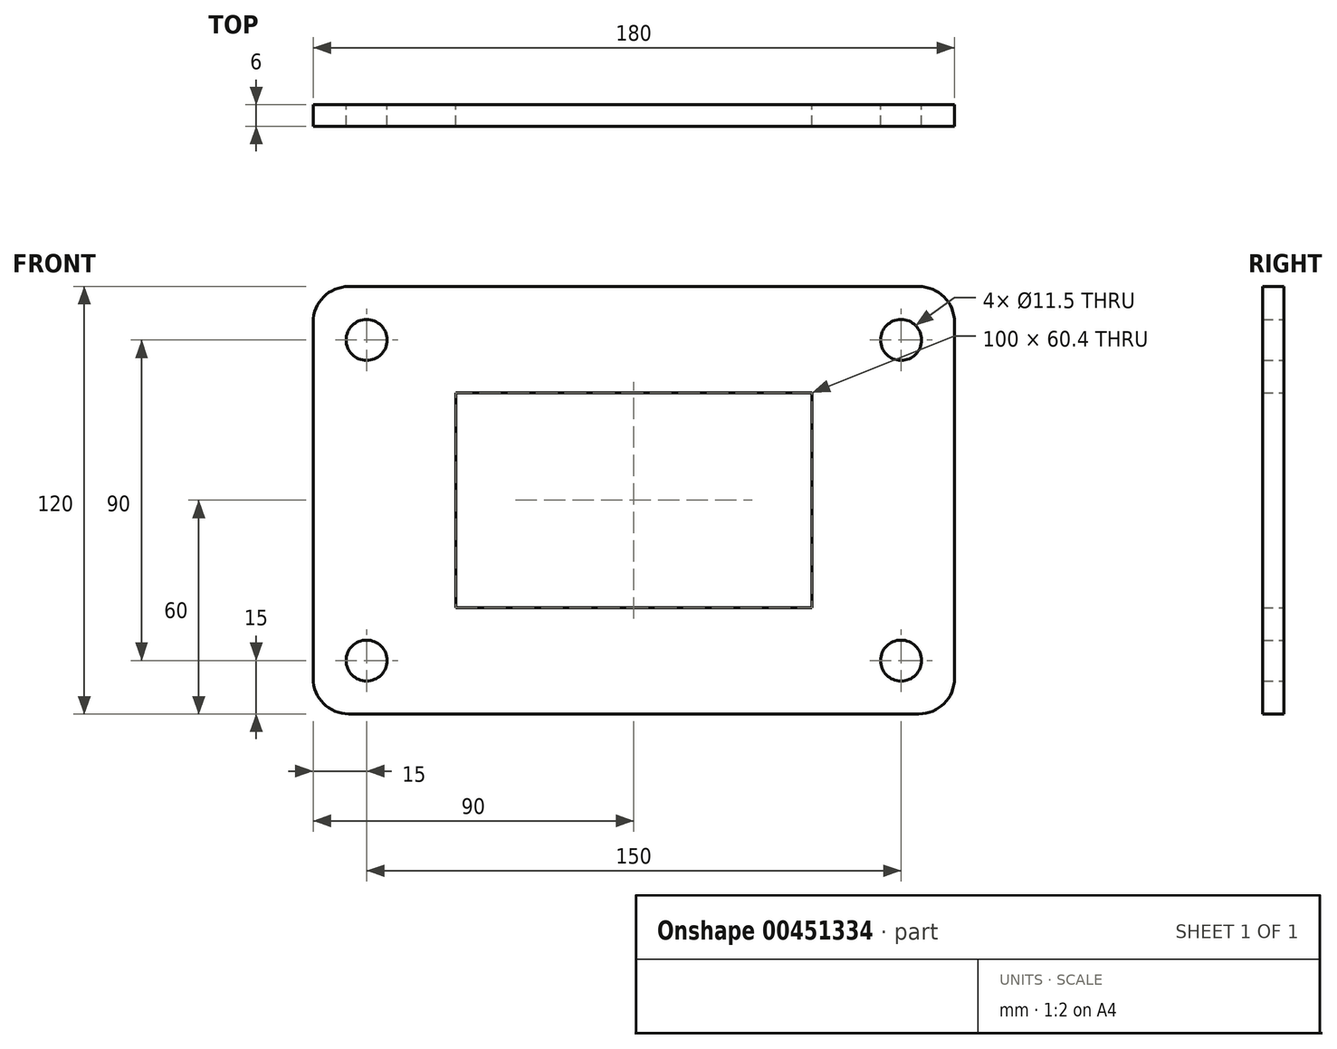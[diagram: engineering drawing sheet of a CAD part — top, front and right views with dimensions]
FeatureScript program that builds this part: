
annotation { "Feature Type Name" : "Feature", "Feature Type Description" : "" }
export const myFeature = defineFeature(function(context is Context, id is Id, definition is map)
    precondition{}
    {
        {
            var Q0;
            Q0=qCreatedBy(makeId("Front.planeOp"),FACE);
            var sketch = newSketch(context, id + "F0", { "sketchPlane" : qUnion([Q0])});
            skLineSegment(sketch, "E0.bottom", {"start": v(90, 60) * mm, "end": v(-90, 60) * mm});
            skLineSegment(sketch, "E0.top", {"start": v(90, -60) * mm, "end": v(-90, -60) * mm});
            skLineSegment(sketch, "E0.left", {"start": v(90, 60) * mm, "end": v(90, -60) * mm});
            skLineSegment(sketch, "E0.right", {"start": v(-90, 60) * mm, "end": v(-90, -60) * mm});
            skPoint(sketch, "E0.middle", {"position": v(0, 0) * mm});
            skLineSegment(sketch, "E1.bottom", {"start": v(50, 30.2) * mm, "end": v(-50, 30.2) * mm});
            skLineSegment(sketch, "E1.top", {"start": v(50, -30.2) * mm, "end": v(-50, -30.2) * mm});
            skLineSegment(sketch, "E1.left", {"start": v(50, 30.2) * mm, "end": v(50, -30.2) * mm});
            skLineSegment(sketch, "E1.right", {"start": v(-50, 30.2) * mm, "end": v(-50, -30.2) * mm});
            skCircle(sketch, "E2", {"center": v(-75, 45) * mm, "radius": 5.75 * mm});
            skCircle(sketch, "E3", {"center": v(-75, -45) * mm, "radius": 5.75 * mm});
            skCircle(sketch, "E4.MirrorC", {"center": v(75, -45) * mm, "radius": 5.75 * mm});
            skCircle(sketch, "E5.MirrorC", {"center": v(75, 45) * mm, "radius": 5.75 * mm});
            skSolve(sketch);
        }
        {
            var Q0;
            Q0=makeQuery(id+"F0.imprint","IMPRINT",FACE,{"disambiguationData":[TD([[makeQuery(id+"F0.imprint","IMPRINT",EDGE,{"derivedFrom":sQuery(id+"F0.wireOp",EDGE,"E0.bottom")}),1.0]])]});
            extrude(context, id + "F1", {"entities" : qUnion([Q0]), "depth" : 6 * mm});
        }
        {
            var Q0;
            Q0=makeQuery(id+"F1.opExtrude","SWEPT_EDGE",EDGE,{"disambiguationData":[OSD([sQuery(id+"F0.wireOp",EDGE,"E0.bottom"),sQuery(id+"F0.wireOp",EDGE,"E0.right")])]});
            var Q1;
            Q1=makeQuery(id+"F1.opExtrude","SWEPT_EDGE",EDGE,{"disambiguationData":[OSD([sQuery(id+"F0.wireOp",EDGE,"E0.bottom"),sQuery(id+"F0.wireOp",EDGE,"E0.left")])]});
            var Q2;
            Q2=makeQuery(id+"F1.opExtrude","SWEPT_EDGE",EDGE,{"disambiguationData":[OSD([sQuery(id+"F0.wireOp",EDGE,"E0.top"),sQuery(id+"F0.wireOp",EDGE,"E0.left")])]});
            var Q3;
            Q3=makeQuery(id+"F1.opExtrude","SWEPT_EDGE",EDGE,{"disambiguationData":[OSD([sQuery(id+"F0.wireOp",EDGE,"E0.top"),sQuery(id+"F0.wireOp",EDGE,"E0.right")])]});
            fillet(context, id + "F2", {"entities" : qUnion([Q0, Q1, Q2, Q3]), "radius" : 10 * mm, "tangentPropagation" : true, "allowEdgeOverflow" : false});
        }
    });
